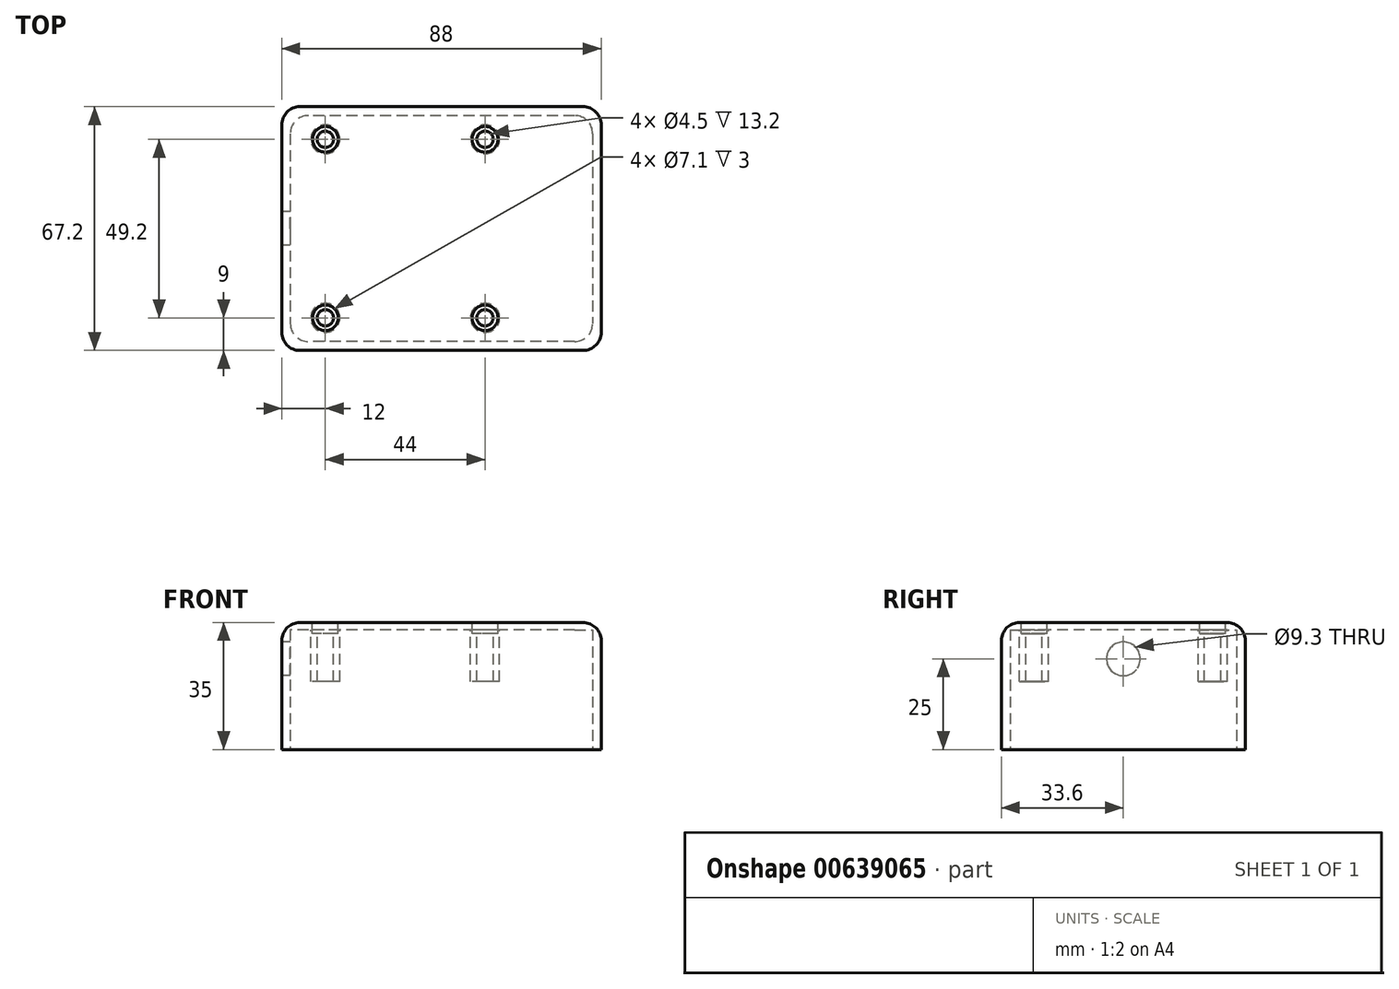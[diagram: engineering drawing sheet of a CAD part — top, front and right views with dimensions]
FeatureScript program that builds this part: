
annotation { "Feature Type Name" : "Feature", "Feature Type Description" : "" }
export const myFeature = defineFeature(function(context is Context, id is Id, definition is map)
    precondition{}
    {
        {
            var Q0;
            Q0=qCreatedBy(makeId("Top.planeOp"),FACE);
            var sketch = newSketch(context, id + "F0", { "sketchPlane" : qUnion([Q0])});
            skLineSegment(sketch, "E0.bottom", {"start": v(-39, 33.6) * mm, "end": v(39, 33.6) * mm});
            skLineSegment(sketch, "E0.top", {"start": v(-39, -33.6) * mm, "end": v(39, -33.6) * mm});
            skLineSegment(sketch, "E0.left", {"start": v(-44, 28.6) * mm, "end": v(-44, -28.6) * mm});
            skLineSegment(sketch, "E0.right", {"start": v(44, 28.6) * mm, "end": v(44, -28.6) * mm});
            skPoint(sketch, "E0.middle", {"position": v(0, 0) * mm});
            skLineSegment(sketch, "E1.bottom", {"start": v(-36.65, 31.15) * mm, "end": v(36.65, 31.15) * mm});
            skLineSegment(sketch, "E1.top", {"start": v(-36.65, -31.15) * mm, "end": v(36.65, -31.15) * mm});
            skLineSegment(sketch, "E1.left", {"start": v(-41.65, 26.15) * mm, "end": v(-41.65, -26.15) * mm});
            skLineSegment(sketch, "E1.right", {"start": v(41.65, 26.15) * mm, "end": v(41.65, -26.15) * mm});
            skPoint(sketch, "E2.visualSharp", {"position": v(-41.65, 31.15) * mm});
            skArc(sketch, "E2.filletArc", {"start": v(-36.65, 31.15) * mm, "mid": v(-40.19, 29.69) * mm, "end": v(-41.65, 26.15) * mm});
            skPoint(sketch, "E3.visualSharp", {"position": v(41.65, 31.15) * mm});
            skArc(sketch, "E3.filletArc", {"start": v(41.65, 26.15) * mm, "mid": v(40.19, 29.69) * mm, "end": v(36.65, 31.15) * mm});
            skPoint(sketch, "E4.visualSharp", {"position": v(-41.65, -31.15) * mm});
            skArc(sketch, "E4.filletArc", {"start": v(-41.65, -26.15) * mm, "mid": v(-40.19, -29.69) * mm, "end": v(-36.65, -31.15) * mm});
            skPoint(sketch, "E5.visualSharp", {"position": v(41.65, -31.15) * mm});
            skArc(sketch, "E5.filletArc", {"start": v(36.65, -31.15) * mm, "mid": v(40.19, -29.69) * mm, "end": v(41.65, -26.15) * mm});
            skPoint(sketch, "E6.visualSharp", {"position": v(44, -33.6) * mm});
            skArc(sketch, "E6.filletArc", {"start": v(39, -33.6) * mm, "mid": v(42.54, -32.14) * mm, "end": v(44, -28.6) * mm});
            skPoint(sketch, "E7.visualSharp", {"position": v(44, 33.6) * mm});
            skArc(sketch, "E7.filletArc", {"start": v(44, 28.6) * mm, "mid": v(42.54, 32.14) * mm, "end": v(39, 33.6) * mm});
            skPoint(sketch, "E8.visualSharp", {"position": v(-44, -33.6) * mm});
            skArc(sketch, "E8.filletArc", {"start": v(-44, -28.6) * mm, "mid": v(-42.54, -32.14) * mm, "end": v(-39, -33.6) * mm});
            skPoint(sketch, "E9.visualSharp", {"position": v(-44, 33.6) * mm});
            skArc(sketch, "E9.filletArc", {"start": v(-39, 33.6) * mm, "mid": v(-42.54, 32.14) * mm, "end": v(-44, 28.6) * mm});
            skSolve(sketch);
        }
        {
            var Q0;
            Q0 = qSketchRegion(id + "F0", true);
            var Q1;
            Q1=makeQuery(id+"F0.imprint","IMPRINT",FACE,{"disambiguationData":[TD([[makeQuery(id+"F0.imprint","IMPRINT",EDGE,{"derivedFrom":sQuery(id+"F0.wireOp",EDGE,"E1.bottom")}),-1.0]])]});
            extrude(context, id + "F1", {"entities" : qUnion([Q0, Q1]), "depth" : 35 * mm, "offsetDistance" : 25 * mm});
        }
        {
            var Q0;
            Q0=qCreatedBy(makeId("Top.planeOp"),FACE);
            var sketch = newSketch(context, id + "F2", { "sketchPlane" : qUnion([Q0])});
            skLineSegment(sketch, "E10.bottom", {"start": v(36.65, 31.15) * mm, "end": v(-36.65, 31.15) * mm});
            skLineSegment(sketch, "E10.top", {"start": v(36.65, -31.15) * mm, "end": v(-36.65, -31.15) * mm});
            skLineSegment(sketch, "E10.left", {"start": v(41.65, 26.15) * mm, "end": v(41.65, -26.15) * mm});
            skLineSegment(sketch, "E10.right", {"start": v(-41.65, 26.15) * mm, "end": v(-41.65, -26.15) * mm});
            skPoint(sketch, "E10.middle", {"position": v(0, 0) * mm});
            skPoint(sketch, "E11.visualSharp", {"position": v(-41.65, -31.15) * mm});
            skArc(sketch, "E11.filletArc", {"start": v(-41.65, -26.15) * mm, "mid": v(-40.19, -29.69) * mm, "end": v(-36.65, -31.15) * mm});
            skPoint(sketch, "E12.visualSharp", {"position": v(41.65, -31.15) * mm});
            skArc(sketch, "E12.filletArc", {"start": v(36.65, -31.15) * mm, "mid": v(40.19, -29.69) * mm, "end": v(41.65, -26.15) * mm});
            skPoint(sketch, "E13.visualSharp", {"position": v(41.65, 31.15) * mm});
            skArc(sketch, "E13.filletArc", {"start": v(41.65, 26.15) * mm, "mid": v(40.19, 29.69) * mm, "end": v(36.65, 31.15) * mm});
            skPoint(sketch, "E14.visualSharp", {"position": v(-41.65, 31.15) * mm});
            skArc(sketch, "E14.filletArc", {"start": v(-36.65, 31.15) * mm, "mid": v(-40.19, 29.69) * mm, "end": v(-41.65, 26.15) * mm});
            skSolve(sketch);
        }
        {
            var Q0;
            Q0 = qSketchRegion(id + "F2", true);
            extrude(context, id + "F3", {"entities" : qUnion([Q0]), "operationType" : NewBodyOperationType.REMOVE, "depth" : 33 * mm, "offsetDistance" : 25 * mm});
        }
        {
            var Q0;
            Q0=makeQuery(id+"F1.opExtrude","CAP_FACE",FACE,{"disambiguationData":[OSD([sQuery(id+"F0.wireOp",EDGE,"E0.bottom"),sQuery(id+"F0.wireOp",EDGE,"E0.top"),sQuery(id+"F0.wireOp",EDGE,"E0.left"),sQuery(id+"F0.wireOp",EDGE,"E0.right"),sQuery(id+"F0.wireOp",EDGE,"E6.filletArc"),sQuery(id+"F0.wireOp",EDGE,"E7.filletArc"),sQuery(id+"F0.wireOp",EDGE,"E8.filletArc"),sQuery(id+"F0.wireOp",EDGE,"E9.filletArc")])],"isStart":false});
            var sketch = newSketch(context, id + "F4", { "sketchPlane" : qUnion([Q0])});
            skCircle(sketch, "E15", {"center": v(-32, 24.6) * mm, "radius": 2.25 * mm});
            skCircle(sketch, "E16", {"center": v(-32, -24.6) * mm, "radius": 2.25 * mm});
            skCircle(sketch, "E17", {"center": v(12, 24.6) * mm, "radius": 2.25 * mm});
            skCircle(sketch, "E18", {"center": v(12, -24.6) * mm, "radius": 2.25 * mm});
            skSolve(sketch);
        }
        {
            var Q0;
            Q0=makeQuery(id+"F4.imprint","IMPRINT",FACE,{"disambiguationData":[TD([[makeQuery(id+"F4.imprint","IMPRINT",EDGE,{"derivedFrom":sQuery(id+"F4.wireOp",EDGE,"E15")}),-1.0]])]});
            var sketch = newSketch(context, id + "F5", { "sketchPlane" : qUnion([Q0])});
            skCircle(sketch, "E19", {"center": v(-32, 24.6) * mm, "radius": 4 * mm});
            skCircle(sketch, "E20", {"center": v(12, 24.6) * mm, "radius": 4 * mm});
            skCircle(sketch, "E21", {"center": v(-32, -24.6) * mm, "radius": 4 * mm});
            skCircle(sketch, "E22", {"center": v(12, -24.6) * mm, "radius": 4 * mm});
            skSolve(sketch);
        }
        {
            var Q0;
            Q0 = qSketchRegion(id + "F5", true);
            extrude(context, id + "F6", {"entities" : qUnion([Q0]), "operationType" : NewBodyOperationType.ADD, "oppositeDirection" : true, "depth" : 16.2 * mm, "offsetDistance" : 25 * mm});
        }
        {
            var Q0;
            Q0 = qSketchRegion(id + "F4", true);
            extrude(context, id + "F7", {"entities" : qUnion([Q0]), "operationType" : NewBodyOperationType.REMOVE, "oppositeDirection" : true, "depth" : 25 * mm, "offsetDistance" : 25 * mm});
        }
        {
            var Q0;
            Q0=makeQuery(id+"F1.opExtrude","CAP_FACE",FACE,{"disambiguationData":[OSD([sQuery(id+"F0.wireOp",EDGE,"E0.bottom"),sQuery(id+"F0.wireOp",EDGE,"E0.top"),sQuery(id+"F0.wireOp",EDGE,"E0.left"),sQuery(id+"F0.wireOp",EDGE,"E0.right"),sQuery(id+"F0.wireOp",EDGE,"E6.filletArc"),sQuery(id+"F0.wireOp",EDGE,"E7.filletArc"),sQuery(id+"F0.wireOp",EDGE,"E8.filletArc"),sQuery(id+"F0.wireOp",EDGE,"E9.filletArc")])],"isStart":false});
            var sketch = newSketch(context, id + "F8", { "sketchPlane" : qUnion([Q0])});
            skCircle(sketch, "E23", {"center": v(-32, 24.6) * mm, "radius": 3.55 * mm});
            skCircle(sketch, "E24", {"center": v(12, 24.6) * mm, "radius": 3.55 * mm});
            skCircle(sketch, "E25", {"center": v(12, -24.6) * mm, "radius": 3.55 * mm});
            skCircle(sketch, "E26", {"center": v(-32, -24.6) * mm, "radius": 3.55 * mm});
            skSolve(sketch);
        }
        {
            var Q0;
            Q0 = qSketchRegion(id + "F8", true);
            extrude(context, id + "F9", {"entities" : qUnion([Q0]), "operationType" : NewBodyOperationType.REMOVE, "oppositeDirection" : true, "depth" : 3 * mm, "offsetDistance" : 25 * mm});
        }
        {
            var Q0;
            Q0=makeQuery(id+"F1.opExtrude","SWEPT_FACE",FACE,{"disambiguationData":[OSD([sQuery(id+"F0.wireOp",EDGE,"E0.left")])]});
            var sketch = newSketch(context, id + "F10", { "sketchPlane" : qUnion([Q0])});
            skCircle(sketch, "E27", {"center": v(0, 25) * mm, "radius": 4.65 * mm});
            skSolve(sketch);
        }
        {
            var Q0;
            Q0 = qSketchRegion(id + "F10", true);
            extrude(context, id + "F11", {"entities" : qUnion([Q0]), "operationType" : NewBodyOperationType.REMOVE, "oppositeDirection" : true, "depth" : 5 * mm, "offsetDistance" : 25 * mm});
        }
        {
            var Q0;
            Q0=makeQuery(id+"F1.opExtrude","CAP_EDGE",EDGE,{"disambiguationData":[OSD([sQuery(id+"F0.wireOp",EDGE,"E0.bottom")])],"isStart":false});
            fillet(context, id + "F12", {"entities" : qUnion([Q0]), "radius" : 5 * mm, "tangentPropagation" : true, "allowEdgeOverflow" : false});
        }
    });
